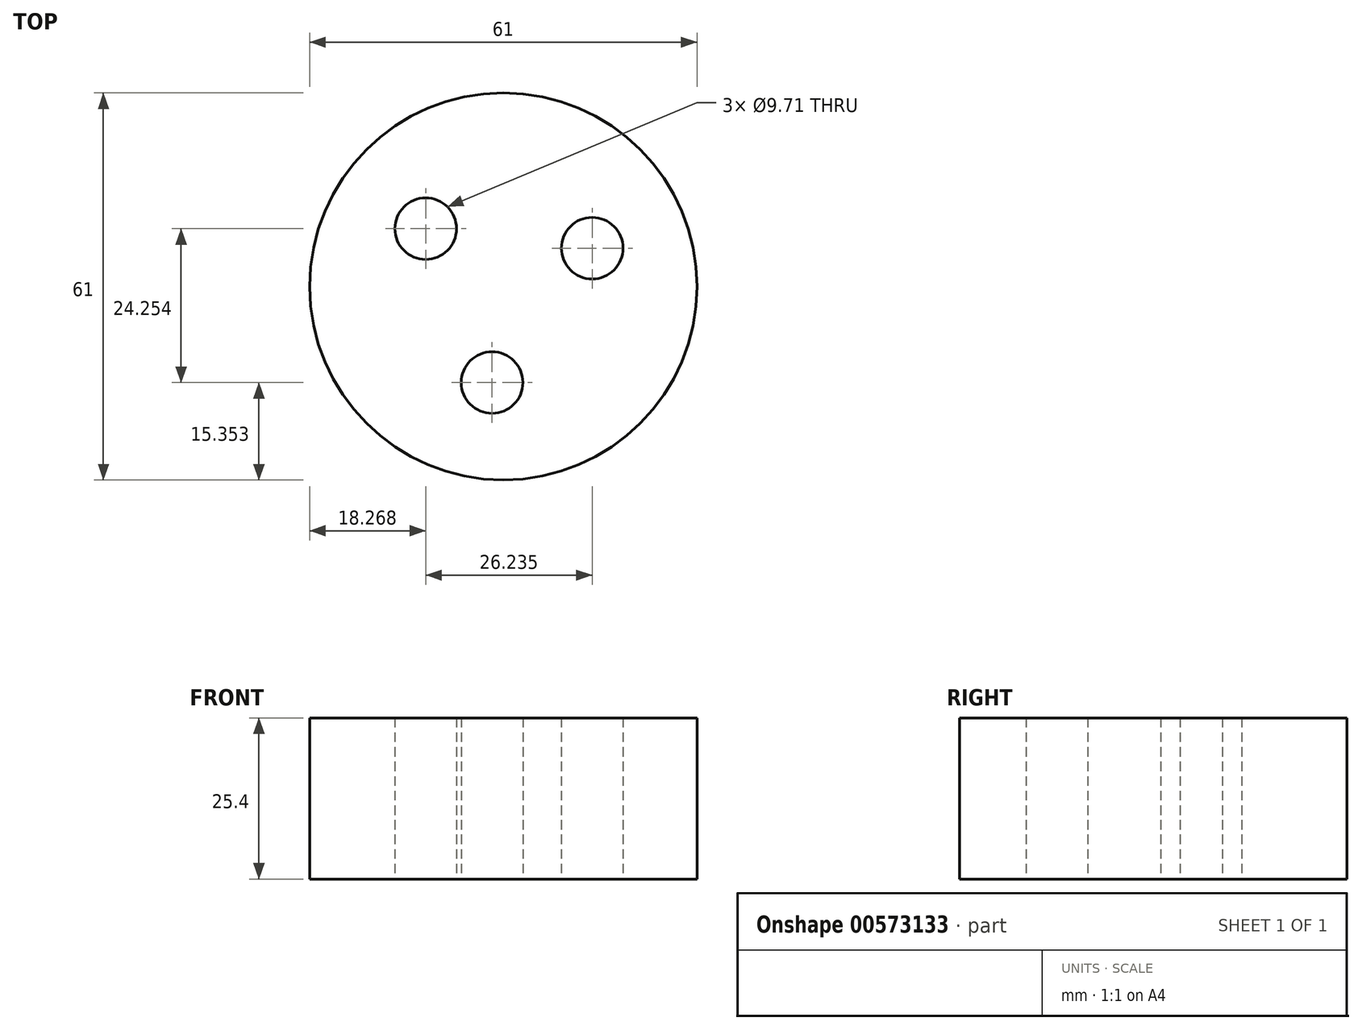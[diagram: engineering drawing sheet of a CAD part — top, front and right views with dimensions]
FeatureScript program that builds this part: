
annotation { "Feature Type Name" : "Feature", "Feature Type Description" : "" }
export const myFeature = defineFeature(function(context is Context, id is Id, definition is map)
    precondition{}
    {
        {
            var Q0;
            Q0=qCreatedBy(makeId("Top.planeOp"),FACE);
            var sketch = newSketch(context, id + "F0", { "sketchPlane" : qUnion([Q0])});
            skCircle(sketch, "E0", {"center": v(0, 0) * mm, "radius": 30.5 * mm});
            skCircle(sketch, "E1", {"center": v(-12.23, 9.1) * mm, "radius": 4.85 * mm});
            skCircle(sketch, "E2.1.0", {"center": v(-1.77, -15.15) * mm, "radius": 4.85 * mm});
            skCircle(sketch, "E2.2.0", {"center": v(14, 6.04) * mm, "radius": 4.85 * mm});
            skSolve(sketch);
        }
        {
            var Q0;
            Q0=makeQuery(id+"F0.imprint","IMPRINT",FACE,{"disambiguationData":[TD([[makeQuery(id+"F0.imprint","IMPRINT",EDGE,{"derivedFrom":sQuery(id+"F0.wireOp",EDGE,"E0")}),1.0]])]});
            extrude(context, id + "F1", {"entities" : qUnion([Q0]), "depth" : 25.4 * mm, "offsetDistance" : 25.4 * mm});
        }
    });
